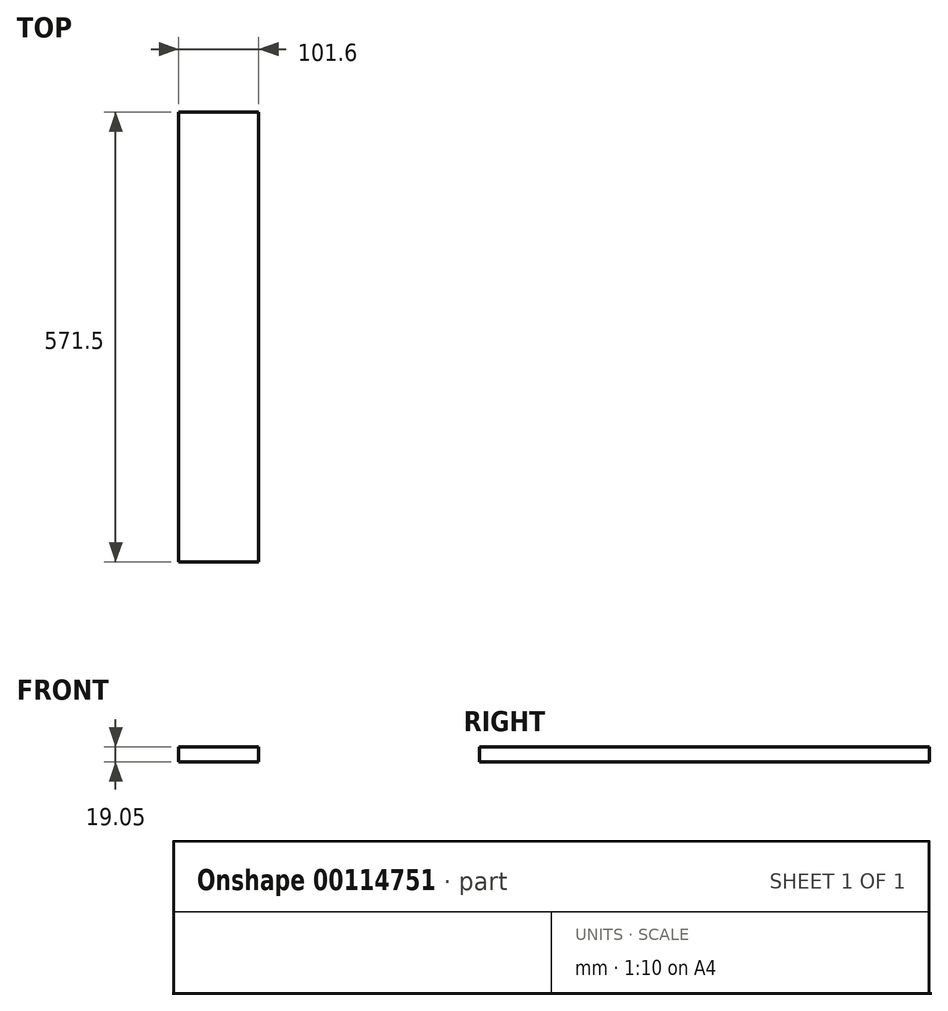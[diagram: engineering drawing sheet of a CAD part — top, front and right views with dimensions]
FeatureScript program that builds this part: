
annotation { "Feature Type Name" : "Feature", "Feature Type Description" : "" }
export const myFeature = defineFeature(function(context is Context, id is Id, definition is map)
    precondition{}
    {
        {
            var Q0;
            Q0=qCreatedBy(makeId("Top.planeOp"),FACE);
            var sketch = newSketch(context, id + "F0", { "sketchPlane" : qUnion([Q0])});
            skLineSegment(sketch, "E0.bottom", {"start": v(0, 0) * mm, "end": v(101.6, 0) * mm});
            skLineSegment(sketch, "E0.top", {"start": v(0, 571.5) * mm, "end": v(101.6, 571.5) * mm});
            skLineSegment(sketch, "E0.left", {"start": v(0, 0) * mm, "end": v(0, 571.5) * mm});
            skLineSegment(sketch, "E0.right", {"start": v(101.6, 0) * mm, "end": v(101.6, 571.5) * mm});
            skSolve(sketch);
        }
        {
            var Q0;
            Q0=qSketchRegion(id+"F0",true);
            extrude(context, id + "F1", {"entities" : qUnion([Q0]), "depth" : 19.05 * mm});
        }
    });
